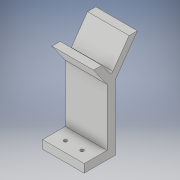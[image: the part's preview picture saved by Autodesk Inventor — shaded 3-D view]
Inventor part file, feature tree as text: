
AUTODESK INVENTOR PART (.ipt)
format: ipt  version: 2019 (Build 230136000, 136)  size: 323,072 bytes
history: native  units: in
note: dims shown in document units (in); Inventor stores cm internally (conversion verified against a paired STEP export)
features: sketch x3, extrude x2, plane x1, loft x1, fillet x1
ambient origin geometry x8: Origin, YZ Plane, XZ Plane, XY Plane, X Axis, Y Axis, Z Axis, Center Point
bodies: Body1 (feature_tree)
feature tree (8):
  plane  "Work Plane1"
  loft  "Loft1"
  fillet  "Fillet1"  Radius=0.0787in
  extrude  "Extrusion2"  Depth=0.1575in
  extrude  "Extrusion3"  Depth=0.1575in
  sketch  "Sketch2"  dims[d7=0.4724in d9=0.0787in d10=0.0787in]
  sketch  "Sketch3"  dims[d12=0.1575in d13=0.7874in]
  sketch  "Sketch4"  dims[d15=0.0041in d19=0.0041in d26=0.3613in d27=0.2501in d30=0.0in d31=90.0deg d32=0.0in d33=90.0deg d34=0.0394in d35=1.2402in d36=0.1575in d37=0.5906in d38=0.1575in d39=0.4331in d40=0.0in d41=0.0in d44=0.1969in d45=0.2362in d46=0.2362in d48=0.1969in d49=0.0624in d50=0.0624in d51=0.3937in d52=0.0in d53=0.4853in d55=0.9942in d56=0.5906in d57=0.1575in d58=0.4899in]
